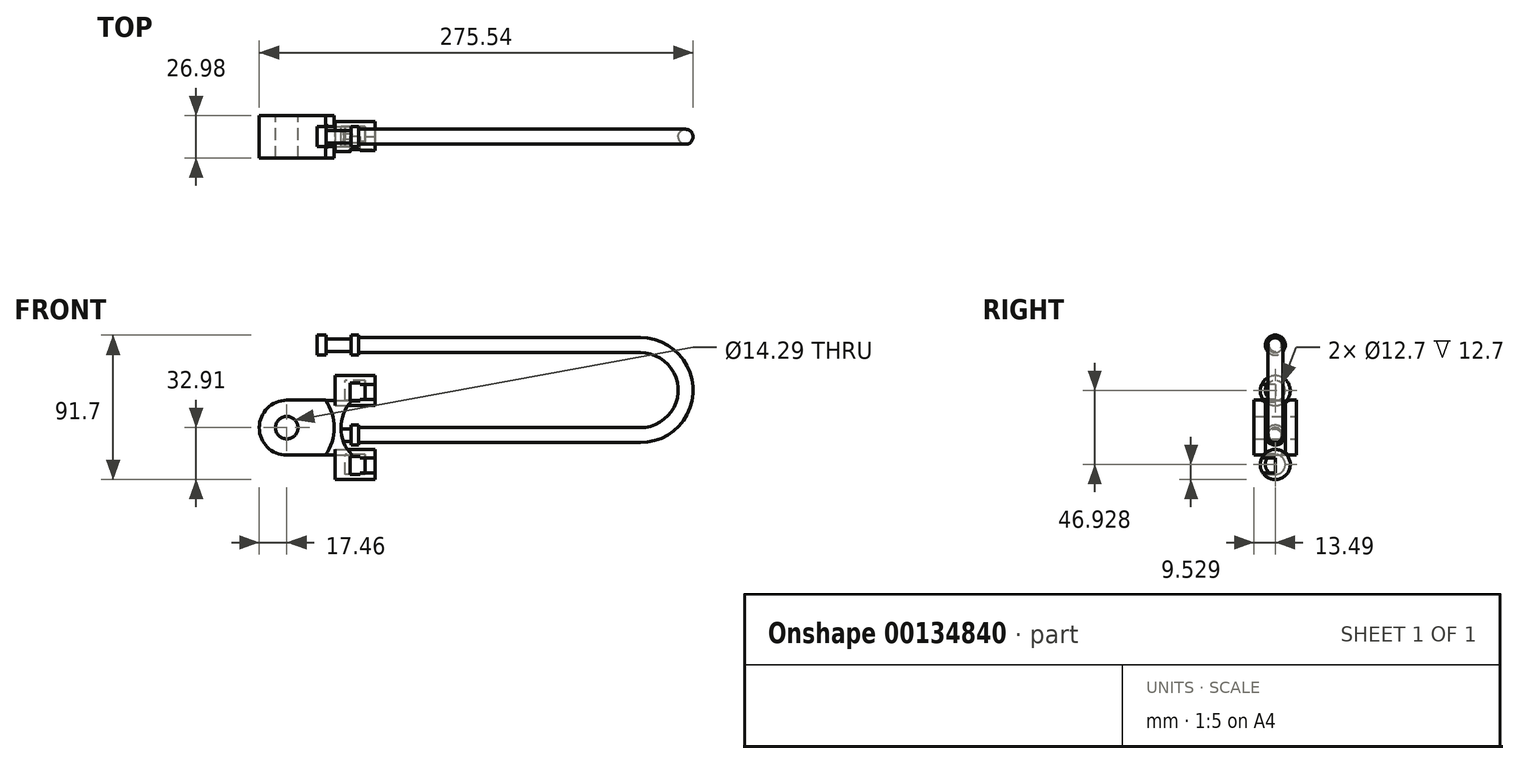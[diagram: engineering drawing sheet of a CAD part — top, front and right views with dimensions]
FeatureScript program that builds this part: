
annotation { "Feature Type Name" : "Feature", "Feature Type Description" : "" }
export const myFeature = defineFeature(function(context is Context, id is Id, definition is map)
    precondition{}
    {
        {
            var Q0;
            Q0=qCreatedBy(makeId("Front.planeOp"),FACE);
            var sketch = newSketch(context, id + "F0", { "sketchPlane" : qUnion([Q0])});
            skCircle(sketch, "E0", {"center": v(0, 0) * mm, "radius": 7.14 * mm});
            skArc(sketch, "E1", {"start": v(0, 17.46) * mm, "mid": v(-17.46, 0) * mm, "end": v(0, -17.46) * mm});
            skLineSegment(sketch, "E2", {"start": v(0, 0) * mm, "end": v(0, 17.46) * mm});
            skLineSegment(sketch, "E3", {"start": v(0, 17.46) * mm, "end": v(24.6, 17.46) * mm});
            skLineSegment(sketch, "E4", {"start": v(0, -17.46) * mm, "end": v(24.6, -17.46) * mm});
            skArc(sketch, "E5.trimOffspring", {"start": v(24.6, -17.46) * mm, "mid": v(30.16, 0) * mm, "end": v(24.6, 17.46) * mm});
            skSolve(sketch);
        }
        {
            var Q0;
            Q0 = qSketchRegion(id + "F0", true);
            extrude(context, id + "F1", {"entities" : qUnion([Q0]), "endBound" : BoundingType.SYMMETRIC, "depth" : 26.99 * mm});
        }
        {
            var Q0;
            Q0=qCreatedBy(makeId("Front.planeOp"),FACE);
            var sketch = newSketch(context, id + "F2", { "sketchPlane" : qUnion([Q0])});
            skArc(sketch, "E6", {"start": v(41.43, 17.45) * mm, "mid": v(34.49, 0) * mm, "end": v(41.43, -17.45) * mm});
            skLineSegment(sketch, "E7", {"start": v(24.62, 17.45) * mm, "end": v(41.43, 17.45) * mm});
            skLineSegment(sketch, "E8.MirrorCS", {"start": v(24.62, -17.45) * mm, "end": v(41.43, -17.45) * mm});
            skPoint(sketch, "E9.orphan", {"position": v(55.53, 17.45) * mm});
            skPoint(sketch, "E10.orphan", {"position": v(55.53, -17.45) * mm});
            skArc(sketch, "E11", {"start": v(24.62, -17.45) * mm, "mid": v(30.1, 0) * mm, "end": v(24.62, 17.45) * mm});
            skSolve(sketch);
        }
        {
            var Q0;
            Q0=qCreatedBy(makeId("Front.planeOp"),FACE);
            var sketch = newSketch(context, id + "F3", { "sketchPlane" : qUnion([Q0])});
            skLineSegment(sketch, "E12", {"start": v(19.38, 52.44) * mm, "end": v(45.6, 52.44) * mm});
            skLineSegment(sketch, "E13", {"start": v(19.38, 52.44) * mm, "end": v(19.38, 58.79) * mm});
            skLineSegment(sketch, "E14.0", {"start": v(19.38, 58.79) * mm, "end": v(24.94, 58.79) * mm});
            skLineSegment(sketch, "E15.0", {"start": v(24.94, 56.4) * mm, "end": v(40.82, 56.4) * mm});
            skLineSegment(sketch, "E16.0", {"start": v(40.82, 56.4) * mm, "end": v(40.82, 58.79) * mm});
            skLineSegment(sketch, "E17.0", {"start": v(45.58, 52.44) * mm, "end": v(45.58, 58.79) * mm});
            skLineSegment(sketch, "E18", {"start": v(40.82, 58.79) * mm, "end": v(45.58, 58.79) * mm});
            skLineSegment(sketch, "E19.trimOffspring", {"start": v(45.58, 56.4) * mm, "end": v(45.6, 56.4) * mm});
            skLineSegment(sketch, "E20", {"start": v(24.94, 58.79) * mm, "end": v(24.94, 56.4) * mm});
            skPoint(sketch, "E21.orphan", {"position": v(19.38, 58.57) * mm});
            skSolve(sketch);
        }
        {
            var Q0;
            {var subQ3=sQuery(id+"F3.wireOp",EDGE,"E13");Q0=makeQuery(id+"F3.imprint","IMPRINT",FACE,{"disambiguationData":[TD([[makeQuery(id+"F3.imprint","IMPRINT",EDGE,{"derivedFrom":subQ3}),-1.0]])]});}
            var Q1;
            Q1=sQuery(id+"F3.wireOp",EDGE,"E12");
            revolve(context, id + "F4", {"entities" : qUnion([Q0]), "axis" : qUnion([Q1]), "revolveType" : RevolveType.FULL});
        }
        {
            var Q0;
            Q0=makeQuery(id+"F4.opRevolve","SWEPT_FACE",FACE,{"disambiguationData":[OSD([sQuery(id+"F3.wireOp",EDGE,"E17.0")])]});
            var sketch = newSketch(context, id + "F5", { "sketchPlane" : qUnion([Q0])});
            skCircle(sketch, "E22", {"center": v(0, 52.44) * mm, "radius": 4.76 * mm});
            skSolve(sketch);
        }
        {
            var Q0;
            Q0=qCreatedBy(makeId("Front.planeOp"),FACE);
            var sketch = newSketch(context, id + "F6", { "sketchPlane" : qUnion([Q0])});
            skLineSegment(sketch, "E23", {"start": v(45.58, 52.44) * mm, "end": v(224.75, 52.44) * mm});
            skLineSegment(sketch, "E24", {"start": v(224.75, -4.71) * mm, "end": v(45.58, -4.71) * mm});
            skArc(sketch, "E25", {"start": v(224.75, 52.44) * mm, "mid": v(253.32, 23.86) * mm, "end": v(224.75, -4.71) * mm});
            skLineSegment(sketch, "E26", {"start": v(224.75, 23.86) * mm, "end": v(152.36, 23.86) * mm});
            skSolve(sketch);
        }
        {
            var Q0;
            Q0=makeQuery(id+"F5.imprint","IMPRINT",FACE,{"disambiguationData":[TD([[makeQuery(id+"F5.imprint","IMPRINT",EDGE,{"derivedFrom":sQuery(id+"F5.wireOp",EDGE,"E22")}),1.0]])]});
            var Q1;
            Q1=sQuery(id+"F6.wireOp",EDGE,"E23");
            var Q2;
            Q2=sQuery(id+"F6.wireOp",EDGE,"E25");
            var Q3;
            Q3=sQuery(id+"F6.wireOp",EDGE,"E24");
            sweep(context, id + "F7", {"profiles" : qUnion([Q0]), "path" : qUnion([Q1, Q2, Q3])});
        }
        {
            var Q0;
            Q0=makeQuery(id+"F4.opRevolve","SWEPT_BODY",BODY,{"disambiguationData":[OSD([sQuery(id+"F3.wireOp",EDGE,"E12"),sQuery(id+"F3.wireOp",EDGE,"E13"),sQuery(id+"F3.wireOp",EDGE,"E14.0"),sQuery(id+"F3.wireOp",EDGE,"E15.0"),sQuery(id+"F3.wireOp",EDGE,"E16.0"),sQuery(id+"F3.wireOp",EDGE,"E17.0"),sQuery(id+"F3.wireOp",EDGE,"E18"),sQuery(id+"F3.wireOp",EDGE,"E20")])]});
            transform(context, id + "F8", {"entities" : qUnion([Q0]), "transformType" : TransformType.TRANSLATION_3D, "dx" : 0 * mm, "dy" : 0 * mm, "dz" : -57.15 * mm, "makeCopy" : true});
        }
        {
            var Q0;
            Q0=qCreatedBy(makeId("Front.planeOp"),FACE);
            var sketch = newSketch(context, id + "F9", { "sketchPlane" : qUnion([Q0])});
            skLineSegment(sketch, "E27", {"start": v(24.5, 17.88) * mm, "end": v(56.15, 17.88) * mm});
            skSolve(sketch);
        }
        {
            var Q0;
            Q0=makeQuery(id+"F2.imprint","IMPRINT",FACE,{"disambiguationData":[TD([[makeQuery(id+"F2.imprint","IMPRINT",EDGE,{"derivedFrom":sQuery(id+"F2.wireOp",EDGE,"E6")}),-1.0]])]});
            extrude(context, id + "F10", {"entities" : qUnion([Q0]), "operationType" : NewBodyOperationType.ADD, "endBound" : BoundingType.SYMMETRIC, "depth" : 12.7 * mm});
        }
        {
            var Q0;
            Q0=makeQuery(id+"F10.boolean.opBoolean","INTERSECT",EDGE,{"derivedFrom":[makeQuery(id+"F1.opExtrude","SWEPT_FACE",FACE,{"disambiguationData":[OSD([sQuery(id+"F0.wireOp",EDGE,"E5.trimOffspring")])]}),makeQuery(id+"F10.opExtrude","CAP_FACE",FACE,{"disambiguationData":[OSD([sQuery(id+"F2.wireOp",EDGE,"E6"),sQuery(id+"F2.wireOp",EDGE,"E7"),sQuery(id+"F2.wireOp",EDGE,"E8.MirrorCS"),sQuery(id+"F2.wireOp",EDGE,"E11")])],"isStart":false})]});
            var Q1;
            Q1=makeQuery(id+"F10.boolean.opBoolean","INTERSECT",EDGE,{"derivedFrom":[makeQuery(id+"F1.opExtrude","SWEPT_FACE",FACE,{"disambiguationData":[OSD([sQuery(id+"F0.wireOp",EDGE,"E5.trimOffspring")])]}),makeQuery(id+"F10.opExtrude","CAP_FACE",FACE,{"disambiguationData":[OSD([sQuery(id+"F2.wireOp",EDGE,"E6"),sQuery(id+"F2.wireOp",EDGE,"E7"),sQuery(id+"F2.wireOp",EDGE,"E8.MirrorCS"),sQuery(id+"F2.wireOp",EDGE,"E11")])],"isStart":true})]});
            fillet(context, id + "F11", {"entities" : qUnion([Q0, Q1]), "radius" : 1.59 * mm, "tangentPropagation" : true, "allowEdgeOverflow" : false});
        }
        {
            var Q0;
            Q0=qCreatedBy(makeId("Right.planeOp"),FACE);
            var Q1;
            Q1=sQuery(id+"F9.wireOp",VERTEX,"E27.end");
            cPlane(context, id + "F12", {"entities" : qUnion([Q0, Q1]), "cplaneType" : CPlaneType.PLANE_POINT, "offset" : 25.4 * mm, "width" : 152.4 * mm, "height" : 152.4 * mm});
        }
        {
            var Q0;
            Q0=qCreatedBy(id+"F12.planeOp",FACE);
            var sketch = newSketch(context, id + "F13", { "sketchPlane" : qUnion([Q0])});
            skCircle(sketch, "E28", {"center": v(0, 28.58) * mm, "radius": 9.53 * mm});
            skSolve(sketch);
        }
        {
            var Q0;
            Q0 = qSketchRegion(id + "F13", true);
            extrude(context, id + "F14", {"entities" : qUnion([Q0]), "oppositeDirection" : true, "depth" : 25.4 * mm});
        }
        {
            var Q0;
            Q0=makeQuery(id+"F14.opExtrude","SWEPT_BODY",BODY,{"disambiguationData":[OSD([sQuery(id+"F13.wireOp",EDGE,"E28")])]});
            transform(context, id + "F15", {"entities" : qUnion([Q0]), "transformType" : TransformType.TRANSLATION_3D, "dx" : 0 * mm, "dy" : 0 * mm, "dz" : -5.03 * mm, "makeCopy" : false});
        }
        {
            var Q0;
            Q0=qCreatedBy(id+"F12.planeOp",FACE);
            cPlane(context, id + "F16", {"entities" : qUnion([Q0]), "cplaneType" : CPlaneType.OFFSET, "offset" : 12.7 * mm, "oppositeDirection" : true, "width" : 152.4 * mm, "height" : 152.4 * mm});
        }
        {
            var Q0;
            Q0=qCreatedBy(id+"F16.planeOp",FACE);
            var sketch = newSketch(context, id + "F17", { "sketchPlane" : qUnion([Q0])});
            skCircle(sketch, "E29", {"center": v(0, 23.55) * mm, "radius": 6.35 * mm});
            skSolve(sketch);
        }
        {
            var Q0;
            Q0 = qSketchRegion(id + "F17", true);
            extrude(context, id + "F18", {"entities" : qUnion([Q0]), "operationType" : NewBodyOperationType.REMOVE, "endBound" : BoundingType.SYMMETRIC, "depth" : 12.7 * mm});
        }
        {
            var Q0;
            Q0=qCreatedBy(makeId("Front.planeOp"),FACE);
            var sketch = newSketch(context, id + "F19", { "sketchPlane" : qUnion([Q0])});
            skLineSegment(sketch, "E30", {"start": v(40.3, 28.51) * mm, "end": v(40.3, 17.1) * mm});
            skLineSegment(sketch, "E31", {"start": v(40.3, 17.1) * mm, "end": v(46.65, 17.1) * mm});
            skLineSegment(sketch, "E32", {"start": v(46.65, 17.1) * mm, "end": v(46.65, 18.04) * mm});
            skLineSegment(sketch, "E33", {"start": v(46.65, 28.51) * mm, "end": v(40.3, 28.51) * mm});
            skLineSegment(sketch, "E34.0", {"start": v(46.65, 18.04) * mm, "end": v(56.81, 18.04) * mm});
            skLineSegment(sketch, "E35.0", {"start": v(46.65, 27.57) * mm, "end": v(56.81, 27.57) * mm});
            skLineSegment(sketch, "E36", {"start": v(56.81, 27.57) * mm, "end": v(56.81, 18.04) * mm});
            skLineSegment(sketch, "E37.trimOffspring", {"start": v(46.65, 27.57) * mm, "end": v(46.65, 28.51) * mm});
            skPoint(sketch, "E38.start.orphan", {"position": v(46.65, 22.8) * mm});
            skSolve(sketch);
        }
        {
            var Q0;
            Q0 = qSketchRegion(id + "F19", true);
            extrude(context, id + "F20", {"entities" : qUnion([Q0]), "operationType" : NewBodyOperationType.REMOVE, "depth" : 25.4 * mm});
        }
        {
            var Q0;
            Q0=makeQuery(id+"F14.opExtrude","SWEPT_BODY",BODY,{"disambiguationData":[OSD([sQuery(id+"F13.wireOp",EDGE,"E28")])]});
            transform(context, id + "F21", {"entities" : qUnion([Q0]), "transformType" : TransformType.TRANSLATION_3D, "dx" : 0 * mm, "dy" : 0 * mm, "dz" : -46.93 * mm, "makeCopy" : true});
        }
    });
